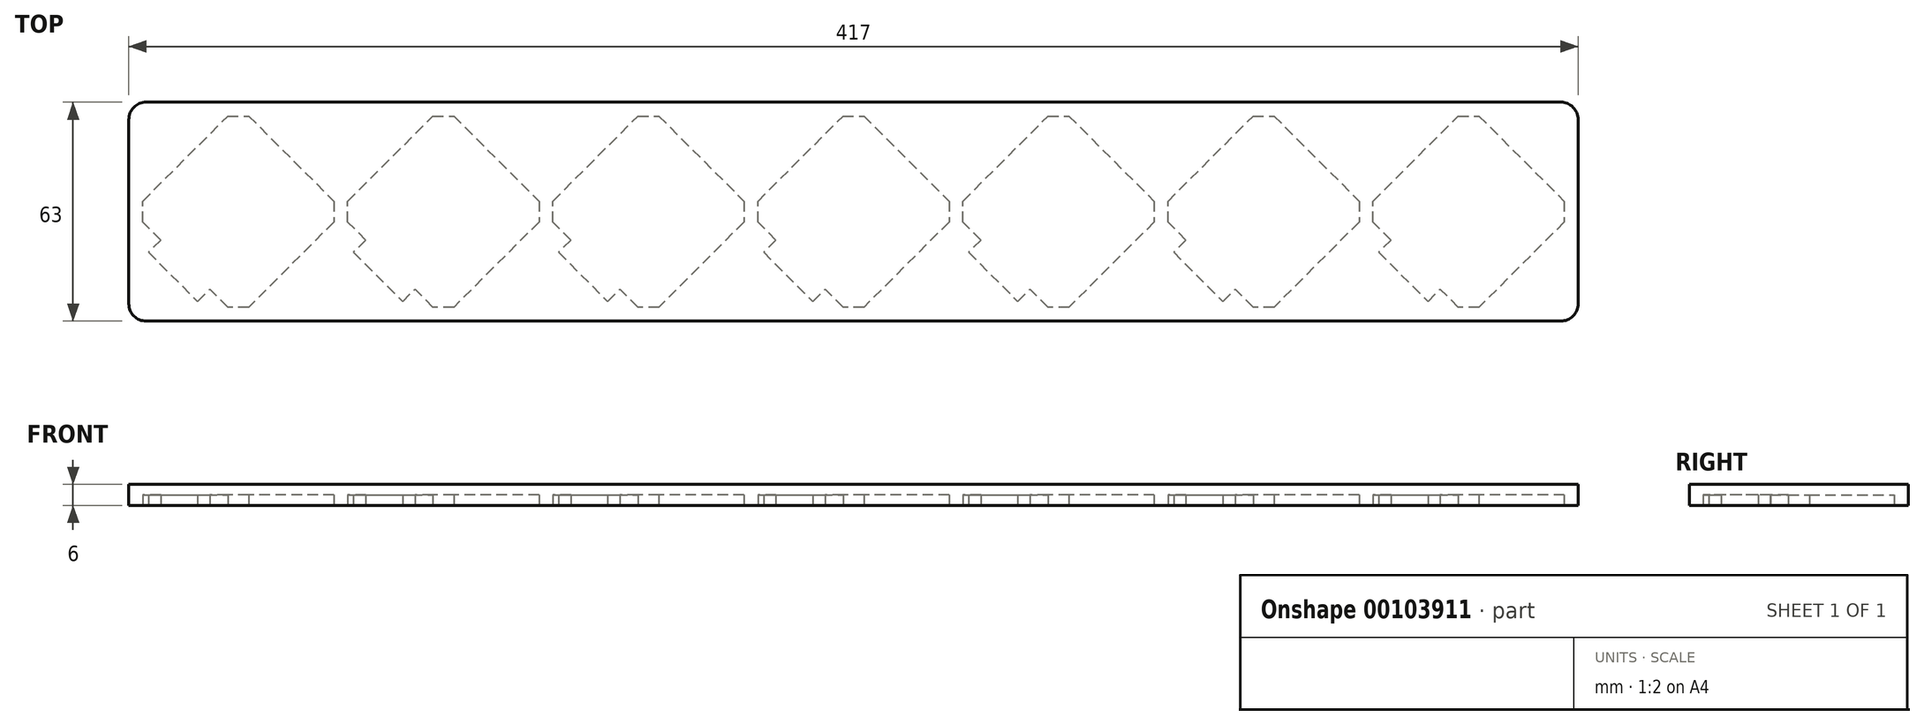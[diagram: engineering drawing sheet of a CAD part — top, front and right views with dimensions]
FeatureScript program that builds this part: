
annotation { "Feature Type Name" : "Feature", "Feature Type Description" : "" }
export const myFeature = defineFeature(function(context is Context, id is Id, definition is map)
    precondition{}
    {
        {
            var Q0;
            Q0=qCreatedBy(makeId("Top.planeOp"),FACE);
            var sketch = newSketch(context, id + "F0", { "sketchPlane" : qUnion([Q0])});
            skLineSegment(sketch, "E0.bottom", {"start": v(-132.07, 63) * mm, "end": v(284.93, 63) * mm});
            skLineSegment(sketch, "E0.top", {"start": v(-132.07, 0) * mm, "end": v(284.93, 0) * mm});
            skLineSegment(sketch, "E0.left", {"start": v(-132.07, 63) * mm, "end": v(-132.07, 0) * mm});
            skLineSegment(sketch, "E0.right", {"start": v(284.93, 63) * mm, "end": v(284.93, 0) * mm});
            skSolve(sketch);
        }
        {
            var Q0;
            Q0=qCreatedBy(makeId("Top.planeOp"),FACE);
            var sketch = newSketch(context, id + "F1", { "sketchPlane" : qUnion([Q0])});
            skLineSegment(sketch, "E1", {"start": v(225.93, 34.5) * mm, "end": v(250.43, 59) * mm});
            skLineSegment(sketch, "E2", {"start": v(250.43, 59) * mm, "end": v(256.43, 59) * mm});
            skLineSegment(sketch, "E3", {"start": v(256.43, 59) * mm, "end": v(280.93, 34.5) * mm});
            skLineSegment(sketch, "E4", {"start": v(280.93, 34.5) * mm, "end": v(280.93, 28.5) * mm});
            skLineSegment(sketch, "E5", {"start": v(280.93, 28.5) * mm, "end": v(256.43, 4) * mm});
            skLineSegment(sketch, "E6", {"start": v(256.43, 4) * mm, "end": v(250.43, 4) * mm});
            skLineSegment(sketch, "E7", {"start": v(250.43, 4) * mm, "end": v(225.93, 28.5) * mm});
            skLineSegment(sketch, "E8", {"start": v(225.93, 28.5) * mm, "end": v(225.93, 34.5) * mm});
            skSolve(sketch);
        }
        {
            var Q0;
            Q0=qCreatedBy(makeId("Top.planeOp"),FACE);
            var sketch = newSketch(context, id + "F2", { "sketchPlane" : qUnion([Q0])});
            skLineSegment(sketch, "E9", {"start": v(166.93, 34.5) * mm, "end": v(191.43, 59) * mm});
            skLineSegment(sketch, "E10", {"start": v(191.43, 59) * mm, "end": v(197.43, 59) * mm});
            skLineSegment(sketch, "E11", {"start": v(197.43, 59) * mm, "end": v(221.93, 34.5) * mm});
            skLineSegment(sketch, "E12", {"start": v(221.93, 34.5) * mm, "end": v(221.93, 28.5) * mm});
            skLineSegment(sketch, "E13", {"start": v(221.93, 28.5) * mm, "end": v(197.43, 4) * mm});
            skLineSegment(sketch, "E14", {"start": v(197.43, 4) * mm, "end": v(191.43, 4) * mm});
            skLineSegment(sketch, "E15", {"start": v(191.43, 4) * mm, "end": v(166.93, 28.5) * mm});
            skLineSegment(sketch, "E16", {"start": v(166.93, 28.5) * mm, "end": v(166.93, 34.5) * mm});
            skSolve(sketch);
        }
        {
            var Q0;
            Q0=qCreatedBy(makeId("Top.planeOp"),FACE);
            var sketch = newSketch(context, id + "F3", { "sketchPlane" : qUnion([Q0])});
            skLineSegment(sketch, "E17", {"start": v(107.93, 34.5) * mm, "end": v(132.43, 59) * mm});
            skLineSegment(sketch, "E18", {"start": v(132.43, 59) * mm, "end": v(138.43, 59) * mm});
            skLineSegment(sketch, "E19", {"start": v(138.43, 59) * mm, "end": v(162.93, 34.5) * mm});
            skLineSegment(sketch, "E20", {"start": v(162.93, 34.5) * mm, "end": v(162.93, 28.5) * mm});
            skLineSegment(sketch, "E21", {"start": v(162.93, 28.5) * mm, "end": v(138.43, 4) * mm});
            skLineSegment(sketch, "E22", {"start": v(138.43, 4) * mm, "end": v(132.43, 4) * mm});
            skLineSegment(sketch, "E23", {"start": v(132.43, 4) * mm, "end": v(107.93, 28.5) * mm});
            skLineSegment(sketch, "E24", {"start": v(107.93, 28.5) * mm, "end": v(107.93, 34.5) * mm});
            skSolve(sketch);
        }
        {
            var Q0;
            Q0=qCreatedBy(makeId("Top.planeOp"),FACE);
            var sketch = newSketch(context, id + "F4", { "sketchPlane" : qUnion([Q0])});
            skLineSegment(sketch, "E25", {"start": v(48.93, 34.5) * mm, "end": v(73.43, 59) * mm});
            skLineSegment(sketch, "E26", {"start": v(73.43, 59) * mm, "end": v(79.43, 59) * mm});
            skLineSegment(sketch, "E27", {"start": v(79.43, 59) * mm, "end": v(103.93, 34.5) * mm});
            skLineSegment(sketch, "E28", {"start": v(103.93, 34.5) * mm, "end": v(103.93, 28.5) * mm});
            skLineSegment(sketch, "E29", {"start": v(103.93, 28.5) * mm, "end": v(79.43, 4) * mm});
            skLineSegment(sketch, "E30", {"start": v(79.43, 4) * mm, "end": v(73.43, 4) * mm});
            skLineSegment(sketch, "E31", {"start": v(73.43, 4) * mm, "end": v(48.93, 28.5) * mm});
            skLineSegment(sketch, "E32", {"start": v(48.93, 28.5) * mm, "end": v(48.93, 34.5) * mm});
            skSolve(sketch);
        }
        {
            var Q0;
            Q0=qCreatedBy(makeId("Top.planeOp"),FACE);
            var sketch = newSketch(context, id + "F5", { "sketchPlane" : qUnion([Q0])});
            skLineSegment(sketch, "E33", {"start": v(-10.07, 34.5) * mm, "end": v(14.43, 59) * mm});
            skLineSegment(sketch, "E34", {"start": v(14.43, 59) * mm, "end": v(20.43, 59) * mm});
            skLineSegment(sketch, "E35", {"start": v(20.43, 59) * mm, "end": v(44.93, 34.5) * mm});
            skLineSegment(sketch, "E36", {"start": v(44.93, 34.5) * mm, "end": v(44.93, 28.5) * mm});
            skLineSegment(sketch, "E37", {"start": v(44.93, 28.5) * mm, "end": v(20.43, 4) * mm});
            skLineSegment(sketch, "E38", {"start": v(20.43, 4) * mm, "end": v(14.43, 4) * mm});
            skLineSegment(sketch, "E39", {"start": v(14.43, 4) * mm, "end": v(-10.07, 28.5) * mm});
            skLineSegment(sketch, "E40", {"start": v(-10.07, 28.5) * mm, "end": v(-10.07, 34.5) * mm});
            skSolve(sketch);
        }
        {
            var Q0;
            Q0=qCreatedBy(makeId("Top.planeOp"),FACE);
            var sketch = newSketch(context, id + "F6", { "sketchPlane" : qUnion([Q0])});
            skLineSegment(sketch, "E41", {"start": v(-69.07, 34.5) * mm, "end": v(-44.57, 59) * mm});
            skLineSegment(sketch, "E42", {"start": v(-44.57, 59) * mm, "end": v(-38.57, 59) * mm});
            skLineSegment(sketch, "E43", {"start": v(-38.57, 59) * mm, "end": v(-14.07, 34.5) * mm});
            skLineSegment(sketch, "E44", {"start": v(-14.07, 34.5) * mm, "end": v(-14.07, 28.5) * mm});
            skLineSegment(sketch, "E45", {"start": v(-14.07, 28.5) * mm, "end": v(-38.57, 4) * mm});
            skLineSegment(sketch, "E46", {"start": v(-38.57, 4) * mm, "end": v(-44.57, 4) * mm});
            skLineSegment(sketch, "E47", {"start": v(-44.57, 4) * mm, "end": v(-69.07, 28.5) * mm});
            skLineSegment(sketch, "E48", {"start": v(-69.07, 28.5) * mm, "end": v(-69.07, 34.5) * mm});
            skSolve(sketch);
        }
        {
            var Q0;
            Q0=qCreatedBy(makeId("Top.planeOp"),FACE);
            var sketch = newSketch(context, id + "F7", { "sketchPlane" : qUnion([Q0])});
            skLineSegment(sketch, "E49", {"start": v(-128.07, 34.5) * mm, "end": v(-103.57, 59) * mm});
            skLineSegment(sketch, "E50", {"start": v(-103.57, 59) * mm, "end": v(-97.57, 59) * mm});
            skLineSegment(sketch, "E51", {"start": v(-97.57, 59) * mm, "end": v(-73.07, 34.5) * mm});
            skLineSegment(sketch, "E52", {"start": v(-73.07, 34.5) * mm, "end": v(-73.07, 28.5) * mm});
            skLineSegment(sketch, "E53", {"start": v(-73.07, 28.5) * mm, "end": v(-97.57, 4) * mm});
            skLineSegment(sketch, "E54", {"start": v(-97.57, 4) * mm, "end": v(-103.57, 4) * mm});
            skLineSegment(sketch, "E55", {"start": v(-103.57, 4) * mm, "end": v(-128.07, 28.5) * mm});
            skLineSegment(sketch, "E56", {"start": v(-128.07, 28.5) * mm, "end": v(-128.07, 34.5) * mm});
            skSolve(sketch);
        }
        {
            var Q0;
            Q0=makeQuery(id+"F0.imprint","IMPRINT",FACE,{"disambiguationData":[TD([[makeQuery(id+"F0.imprint","IMPRINT",EDGE,{"derivedFrom":sQuery(id+"F0.wireOp",EDGE,"E0.bottom")}),-1.0]])]});
            var sketch = newSketch(context, id + "F8", { "sketchPlane" : qUnion([Q0])});
            skLineSegment(sketch, "E57", {"start": v(231.1, 23.32) * mm, "end": v(227.57, 19.79) * mm});
            skLineSegment(sketch, "E58", {"start": v(227.57, 19.79) * mm, "end": v(241.71, 5.64) * mm});
            skLineSegment(sketch, "E59", {"start": v(241.71, 5.64) * mm, "end": v(245.25, 9.18) * mm});
            skLineSegment(sketch, "E60", {"start": v(245.25, 9.18) * mm, "end": v(231.1, 23.32) * mm});
            skSolve(sketch);
        }
        {
            var Q0;
            Q0=makeQuery(id+"F8.imprint","IMPRINT",FACE,{"disambiguationData":[TD([[makeQuery(id+"F8.imprint","IMPRINT",EDGE,{"derivedFrom":sQuery(id+"F8.wireOp",EDGE,"E57")}),-1.0]])]});
            var sketch = newSketch(context, id + "F9", { "sketchPlane" : qUnion([Q0])});
            skLineSegment(sketch, "E61", {"start": v(172.1, 23.33) * mm, "end": v(168.56, 19.8) * mm});
            skLineSegment(sketch, "E62", {"start": v(168.56, 19.8) * mm, "end": v(182.7, 5.66) * mm});
            skLineSegment(sketch, "E63", {"start": v(182.7, 5.66) * mm, "end": v(186.24, 9.2) * mm});
            skLineSegment(sketch, "E64", {"start": v(186.24, 9.2) * mm, "end": v(172.1, 23.33) * mm});
            skSolve(sketch);
        }
        {
            var Q0;
            Q0=makeQuery(id+"F8.imprint","IMPRINT",FACE,{"disambiguationData":[TD([[makeQuery(id+"F8.imprint","IMPRINT",EDGE,{"derivedFrom":sQuery(id+"F8.wireOp",EDGE,"E57")}),-1.0]])]});
            var sketch = newSketch(context, id + "F10", { "sketchPlane" : qUnion([Q0])});
            skLineSegment(sketch, "E65", {"start": v(113.1, 23.33) * mm, "end": v(109.56, 19.8) * mm});
            skLineSegment(sketch, "E66", {"start": v(109.56, 19.8) * mm, "end": v(123.7, 5.66) * mm});
            skLineSegment(sketch, "E67", {"start": v(123.7, 5.66) * mm, "end": v(127.24, 9.2) * mm});
            skLineSegment(sketch, "E68", {"start": v(127.24, 9.2) * mm, "end": v(113.1, 23.33) * mm});
            skSolve(sketch);
        }
        {
            var Q0;
            Q0=makeQuery(id+"F8.imprint","IMPRINT",FACE,{"disambiguationData":[TD([[makeQuery(id+"F8.imprint","IMPRINT",EDGE,{"derivedFrom":sQuery(id+"F8.wireOp",EDGE,"E57")}),-1.0]])]});
            var sketch = newSketch(context, id + "F11", { "sketchPlane" : qUnion([Q0])});
            skLineSegment(sketch, "E69", {"start": v(54.1, 23.32) * mm, "end": v(50.57, 19.79) * mm});
            skLineSegment(sketch, "E70", {"start": v(50.57, 19.79) * mm, "end": v(64.71, 5.64) * mm});
            skLineSegment(sketch, "E71", {"start": v(64.71, 5.64) * mm, "end": v(68.25, 9.18) * mm});
            skLineSegment(sketch, "E72", {"start": v(68.25, 9.18) * mm, "end": v(54.1, 23.32) * mm});
            skSolve(sketch);
        }
        {
            var Q0;
            Q0=makeQuery(id+"F0.imprint","IMPRINT",FACE,{"disambiguationData":[TD([[makeQuery(id+"F0.imprint","IMPRINT",EDGE,{"derivedFrom":sQuery(id+"F0.wireOp",EDGE,"E0.bottom")}),-1.0]])]});
            var sketch = newSketch(context, id + "F12", { "sketchPlane" : qUnion([Q0])});
            skLineSegment(sketch, "E73", {"start": v(-4.9, 23.32) * mm, "end": v(-8.43, 19.79) * mm});
            skLineSegment(sketch, "E74", {"start": v(-8.43, 19.79) * mm, "end": v(5.71, 5.64) * mm});
            skLineSegment(sketch, "E75", {"start": v(5.71, 5.64) * mm, "end": v(9.25, 9.18) * mm});
            skLineSegment(sketch, "E76", {"start": v(9.25, 9.18) * mm, "end": v(-4.9, 23.32) * mm});
            skSolve(sketch);
        }
        {
            var Q0;
            Q0=makeQuery(id+"F8.imprint","IMPRINT",FACE,{"disambiguationData":[TD([[makeQuery(id+"F8.imprint","IMPRINT",EDGE,{"derivedFrom":sQuery(id+"F8.wireOp",EDGE,"E57")}),-1.0]])]});
            var sketch = newSketch(context, id + "F13", { "sketchPlane" : qUnion([Q0])});
            skLineSegment(sketch, "E77", {"start": v(-63.9, 23.32) * mm, "end": v(-67.43, 19.79) * mm});
            skLineSegment(sketch, "E78", {"start": v(-67.43, 19.79) * mm, "end": v(-53.29, 5.64) * mm});
            skLineSegment(sketch, "E79", {"start": v(-53.29, 5.64) * mm, "end": v(-49.75, 9.18) * mm});
            skLineSegment(sketch, "E80", {"start": v(-49.75, 9.18) * mm, "end": v(-63.9, 23.32) * mm});
            skSolve(sketch);
        }
        {
            var Q0;
            Q0=makeQuery(id+"F0.imprint","IMPRINT",FACE,{"disambiguationData":[TD([[makeQuery(id+"F0.imprint","IMPRINT",EDGE,{"derivedFrom":sQuery(id+"F0.wireOp",EDGE,"E0.bottom")}),-1.0]])]});
            var sketch = newSketch(context, id + "F14", { "sketchPlane" : qUnion([Q0])});
            skLineSegment(sketch, "E81", {"start": v(-122.9, 23.32) * mm, "end": v(-126.43, 19.79) * mm});
            skLineSegment(sketch, "E82", {"start": v(-126.43, 19.79) * mm, "end": v(-112.29, 5.64) * mm});
            skLineSegment(sketch, "E83", {"start": v(-112.29, 5.64) * mm, "end": v(-108.75, 9.18) * mm});
            skLineSegment(sketch, "E84", {"start": v(-108.75, 9.18) * mm, "end": v(-122.9, 23.32) * mm});
            skSolve(sketch);
        }
        {
            var Q0;
            Q0=makeQuery(id+"F0.imprint","IMPRINT",FACE,{"disambiguationData":[TD([[makeQuery(id+"F0.imprint","IMPRINT",EDGE,{"derivedFrom":sQuery(id+"F0.wireOp",EDGE,"E0.bottom")}),-1.0]])]});
            extrude(context, id + "F15", {"entities" : qUnion([Q0]), "depth" : 6 * mm});
        }
        {
            var Q0;
            Q0 = qSketchRegion(id + "F1", true);
            var Q1;
            Q1 = qSketchRegion(id + "F2", true);
            var Q2;
            Q2 = qSketchRegion(id + "F3", true);
            var Q3;
            Q3 = qSketchRegion(id + "F4", true);
            var Q4;
            Q4 = qSketchRegion(id + "F5", true);
            var Q5;
            Q5 = qSketchRegion(id + "F6", true);
            var Q6;
            Q6 = qSketchRegion(id + "F7", true);
            var Q7;
            Q7 = qSketchRegion(id + "F8", true);
            var Q8;
            Q8 = qSketchRegion(id + "F9", true);
            var Q9;
            Q9 = qSketchRegion(id + "F10", true);
            var Q10;
            Q10 = qSketchRegion(id + "F11", true);
            var Q11;
            Q11 = qSketchRegion(id + "F12", true);
            var Q12;
            Q12 = qSketchRegion(id + "F13", true);
            var Q13;
            Q13 = qSketchRegion(id + "F14", true);
            extrude(context, id + "F16", {"entities" : qUnion([Q0, Q1, Q2, Q3, Q4, Q5, Q6, Q7, Q8, Q9, Q10, Q11, Q12, Q13]), "operationType" : NewBodyOperationType.REMOVE, "depth" : 3 * mm});
        }
        {
            var Q0;
            Q0=makeQuery(id+"F15.opExtrude","SWEPT_EDGE",EDGE,{"disambiguationData":[OSD([sQuery(id+"F0.wireOp",EDGE,"E0.top"),sQuery(id+"F0.wireOp",EDGE,"E0.right")])]});
            var Q1;
            Q1=makeQuery(id+"F15.opExtrude","SWEPT_EDGE",EDGE,{"disambiguationData":[OSD([sQuery(id+"F0.wireOp",EDGE,"E0.bottom"),sQuery(id+"F0.wireOp",EDGE,"E0.right")])]});
            var Q2;
            Q2=makeQuery(id+"F15.opExtrude","SWEPT_EDGE",EDGE,{"disambiguationData":[OSD([sQuery(id+"F0.wireOp",EDGE,"E0.bottom"),sQuery(id+"F0.wireOp",EDGE,"E0.left")])]});
            var Q3;
            Q3=makeQuery(id+"F15.opExtrude","SWEPT_EDGE",EDGE,{"disambiguationData":[OSD([sQuery(id+"F0.wireOp",EDGE,"E0.top"),sQuery(id+"F0.wireOp",EDGE,"E0.left")])]});
            fillet(context, id + "F17", {"entities" : qUnion([Q0, Q1, Q2, Q3]), "radius" : 5 * mm, "tangentPropagation" : true, "allowEdgeOverflow" : false});
        }
    });
